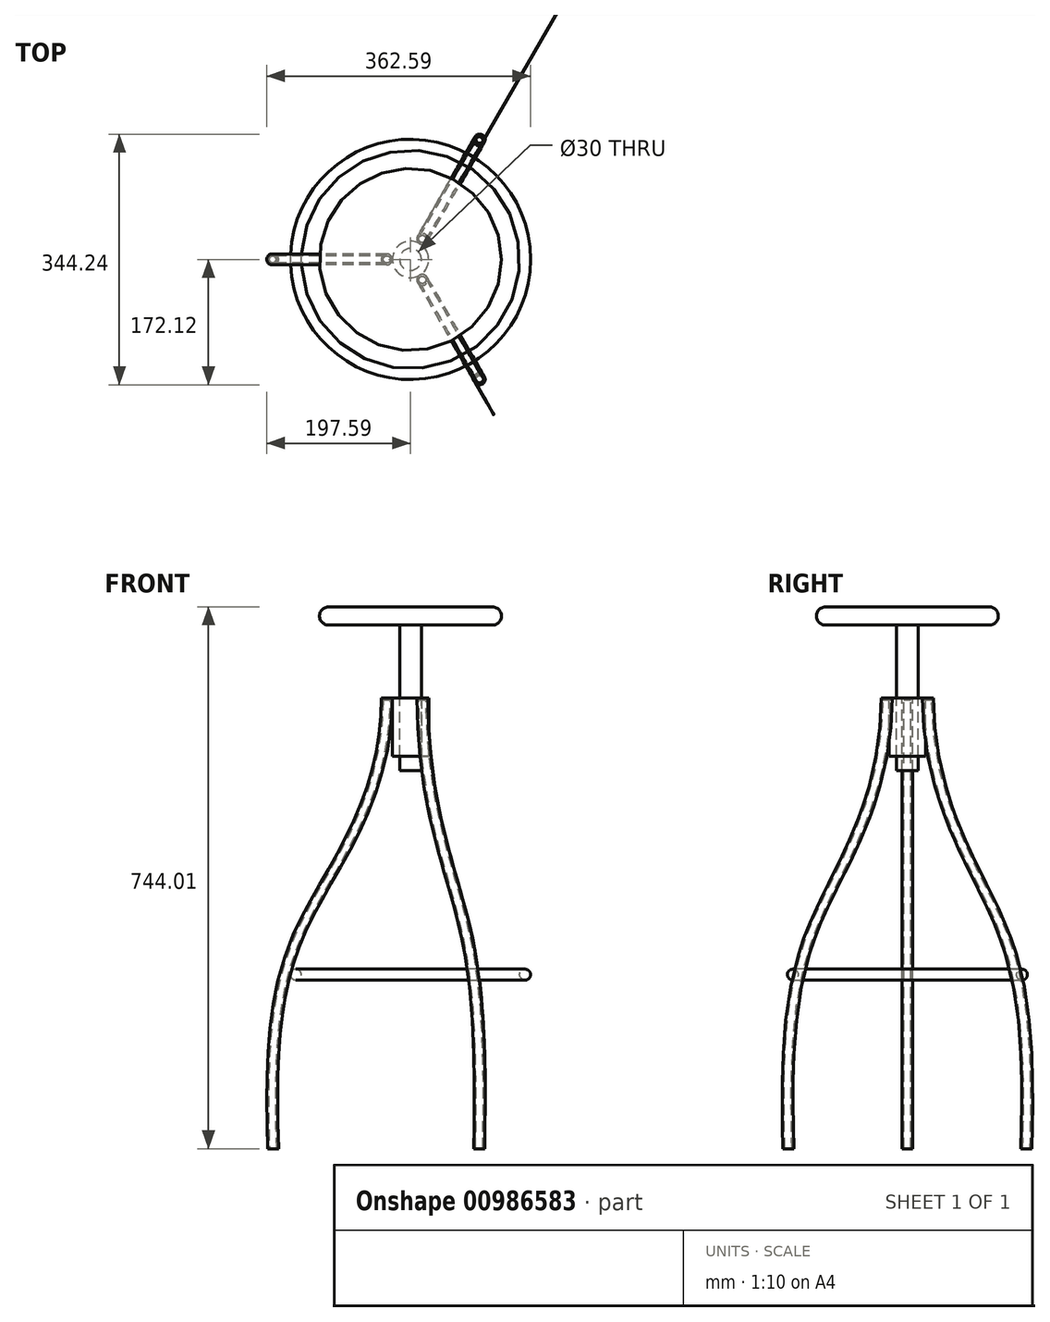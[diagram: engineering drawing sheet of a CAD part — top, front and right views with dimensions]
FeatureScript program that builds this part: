
annotation { "Feature Type Name" : "Feature", "Feature Type Description" : "" }
export const myFeature = defineFeature(function(context is Context, id is Id, definition is map)
    precondition{}
    {
        {
            var Q0;
            Q0=qCreatedBy(makeId("Front.planeOp"),FACE);
            var sketch = newSketch(context, id + "F0", { "sketchPlane" : qUnion([Q0])});
            skFitSpline(sketch, "E0", {"points": [v(-12.39, 0) * mm, v(-129.18, -315.71) * mm, v(-168.72, -619) * mm], "startDerivative": vector(-7.38, -863.02) * mm, "endDerivative": vector(26.98, -851.36) * mm});
            skLineSegment(sketch, "E1", {"start": v(0, 0) * mm, "end": v(0, 358.08) * mm});
            skCircle(sketch, "E2", {"center": v(-157.5, -380) * mm, "radius": 7.5 * mm});
            skSolve(sketch);
        }
        {
            var Q0;
            Q0=qCreatedBy(makeId("Top.planeOp"),FACE);
            var sketch = newSketch(context, id + "F1", { "sketchPlane" : qUnion([Q0])});
            skCircle(sketch, "E3", {"center": v(0, 0) * mm, "radius": 25 * mm});
            skCircle(sketch, "E4", {"center": v(-32.5, 0) * mm, "radius": 7.5 * mm});
            skCircle(sketch, "E5", {"center": v(0, 0) * mm, "radius": 15 * mm});
            skSolve(sketch);
        }
        {
            var Q0;
            Q0=makeQuery(id+"F1.imprint","IMPRINT",FACE,{"disambiguationData":[TD([[makeQuery(id+"F1.imprint","IMPRINT",EDGE,{"derivedFrom":sQuery(id+"F1.wireOp",EDGE,"E4")}),1.0]])]});
            var Q1;
            Q1=sQuery(id+"F0.wireOp",EDGE,"E0");
            sweep(context, id + "F2", {"profiles" : qUnion([Q0]), "path" : qUnion([Q1]), "keepProfileOrientation" : true});
        }
        {
            var Q0;
            Q0=makeQuery(id+"F2.opSweep","CAP_FACE",FACE,{"disambiguationData":[OSD([sQuery(id+"F0.wireOp",VERTEX,"E0.end"),sQuery(id+"F1.wireOp",EDGE,"E4")])],"isStart":false});
            shell(context, id + "F3", {"entities" : qUnion([Q0]), "thickness" : 2.5 * mm});
        }
        {
            var Q0;
            Q0=makeQuery(id+"F2.opSweep","SWEPT_BODY",BODY,{"disambiguationData":[OSD([sQuery(id+"F0.wireOp",EDGE,"E0"),sQuery(id+"F1.wireOp",EDGE,"6TbsQZ08-osyq-xJN1-1fqp-YsgyRUpYaWQY")])]});
            var Q1;
            Q1=sQuery(id+"F0.wireOp",EDGE,"E1");
            circularPattern(context, id + "F4", {"entities" : qUnion([Q0]), "axis" : qUnion([Q1]), "angle" : 360 * degree, "instanceCount" : 3, "equalSpace" : true});
        }
        {
            var Q0;
            Q0=makeQuery(id+"F1.imprint","IMPRINT",FACE,{"disambiguationData":[TD([[makeQuery(id+"F1.imprint","IMPRINT",EDGE,{"derivedFrom":sQuery(id+"F1.wireOp",EDGE,"E3")}),1.0]])]});
            extrude(context, id + "F5", {"entities" : qUnion([Q0]), "oppositeDirection" : true, "depth" : 80 * mm, "offsetDistance" : 25 * mm});
        }
        {
            var Q0;
            Q0=makeQuery(id+"F0.imprint","IMPRINT",FACE,{"disambiguationData":[TD([[makeQuery(id+"F0.imprint","IMPRINT",EDGE,{"derivedFrom":sQuery(id+"F0.wireOp",EDGE,"E2")}),1.0]])]});
            var Q1;
            Q1=sQuery(id+"F0.wireOp",EDGE,"E1");
            revolve(context, id + "F6", {"surfaceOperationType" : NewSurfaceOperationType.NEW, "entities" : qUnion([Q0]), "axis" : qUnion([Q1]), "revolveType" : RevolveType.FULL});
        }
        {
            var Q0;
            Q0=makeQuery(id+"F1.imprint","IMPRINT",FACE,{"disambiguationData":[TD([[makeQuery(id+"F1.imprint","IMPRINT",EDGE,{"derivedFrom":sQuery(id+"F1.wireOp",EDGE,"E5")}),1.0]])]});
            extrude(context, id + "F7", {"entities" : qUnion([Q0]), "endBound" : BoundingType.SYMMETRIC, "depth" : 200 * mm, "offsetDistance" : 25 * mm});
        }
        {
            var Q0;
            Q0=makeQuery(id+"F7.opExtrude","CAP_FACE",FACE,{"disambiguationData":[OSD([sQuery(id+"F1.wireOp",EDGE,"E5")])],"isStart":false});
            var sketch = newSketch(context, id + "F8", { "sketchPlane" : qUnion([Q0])});
            skSolve(sketch);
        }
        {
            var Q0;
            Q0=makeQuery(id+"F8.imprint","IMPRINT",FACE,{"disambiguationData":[TD([[makeQuery(id+"F8.imprint","IMPRINT",EDGE,{"derivedFrom":makeQuery(id+"F7.opExtrude","CAP_EDGE",EDGE,{"disambiguationData":[OSD([sQuery(id+"F1.wireOp",EDGE,"E5")])],"isStart":false})}),1.0]])]});
            var sketch = newSketch(context, id + "F9", { "sketchPlane" : qUnion([Q0])});
            skCircle(sketch, "E6", {"center": v(0, 0) * mm, "radius": 125 * mm});
            skSolve(sketch);
        }
        {
            var Q0;
            Q0=makeQuery(id+"F9.imprint","IMPRINT",FACE,{"disambiguationData":[TD([[makeQuery(id+"F9.imprint","IMPRINT",EDGE,{"derivedFrom":sQuery(id+"F9.wireOp",EDGE,"E6")}),1.0]])]});
            var Q1;
            Q1=makeQuery(id+"F8.imprint","IMPRINT",FACE,{"disambiguationData":[TD([[makeQuery(id+"F8.imprint","IMPRINT",EDGE,{"derivedFrom":makeQuery(id+"F7.opExtrude","CAP_EDGE",EDGE,{"disambiguationData":[OSD([sQuery(id+"F1.wireOp",EDGE,"E5")])],"isStart":false})}),1.0]])]});
            extrude(context, id + "F10", {"entities" : qUnion([Q0, Q1]), "operationType" : NewBodyOperationType.ADD, "depth" : 25 * mm, "offsetDistance" : 25 * mm});
        }
        {
            var Q0;
            Q0=makeQuery(id+"F10.opExtrude","CAP_EDGE",EDGE,{"disambiguationData":[OSD([sQuery(id+"F9.wireOp",EDGE,"E6")])],"isStart":false});
            var Q1;
            Q1=makeQuery(id+"F10.opExtrude","CAP_EDGE",EDGE,{"disambiguationData":[OSD([sQuery(id+"F9.wireOp",EDGE,"E6")])],"isStart":true});
            fillet(context, id + "F11", {"entities" : qUnion([Q0, Q1]), "radius" : 12.5 * mm, "tangentPropagation" : true, "allowEdgeOverflow" : false});
        }
    });
